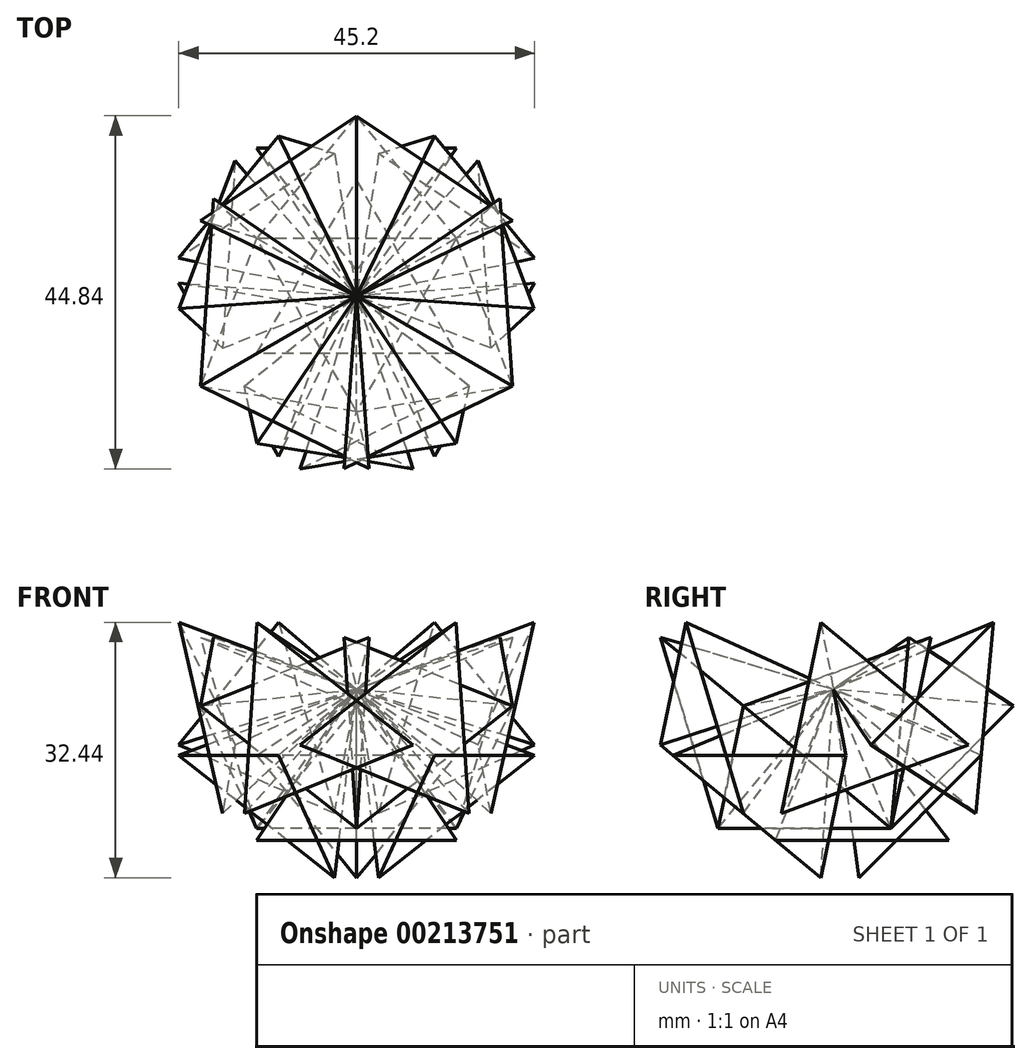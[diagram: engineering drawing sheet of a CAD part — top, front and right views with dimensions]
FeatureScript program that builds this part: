
annotation { "Feature Type Name" : "Feature", "Feature Type Description" : "" }
export const myFeature = defineFeature(function(context is Context, id is Id, definition is map)
    precondition{}
    {
        {
            assignVariable(context, id + "F0", {"name" : "a", "anyValue" : 1});
        }
        {
            assignVariable(context, id + "F1", {"name" : "phi", "anyValue" : getVariable(context, 'a') * (1 + sqrt(5)) / 2});
        }
        {
            assignVariable(context, id + "F2", {"name" : "h", "anyValue" : (sqrt(3) / 3) * (getVariable(context, 'a') + getVariable(context, 'a') * getVariable(context, 'phi'))});
        }
        {
            var Q0;
            Q0=qCreatedBy(makeId("Top.planeOp"),FACE);
            var sketch = newSketch(context, id + "F3", { "sketchPlane" : qUnion([Q0])});
            skCircle(sketch, "E0.cCircle", {"center": v(0, 0) * mm, "radius": 14.66 * mm, "construction": true});
            skLineSegment(sketch, "E0.0", {"start": v(0, 14.66) * mm, "end": v(12.7, -7.33) * mm});
            skLineSegment(sketch, "E0.1", {"start": v(12.7, -7.33) * mm, "end": v(-12.7, -7.33) * mm});
            skLineSegment(sketch, "E0.2", {"start": v(-12.7, -7.33) * mm, "end": v(0, 14.66) * mm});
            skSolve(sketch);
        }
        {
            var Q0;
            Q0=qCreatedBy(makeId("Top.planeOp"),FACE);
            cPlane(context, id + "F4", {"entities" : qUnion([Q0]), "cplaneType" : CPlaneType.OFFSET, "offset" : (getVariable(context, 'h')) * mm, "width" : 152.4 * mm, "height" : 152.4 * mm});
        }
        {
            var Q0;
            Q0=qCreatedBy(id+"F4.planeOp",FACE);
            var sketch = newSketch(context, id + "F5", { "sketchPlane" : qUnion([Q0])});
            skCircle(sketch, "E1.cCircle", {"center": v(0, 0) * mm, "radius": 14.66 * mm, "construction": true});
            skLineSegment(sketch, "E1.0", {"start": v(0, -14.66) * mm, "end": v(-12.7, 7.33) * mm});
            skLineSegment(sketch, "E1.1", {"start": v(-12.7, 7.33) * mm, "end": v(12.7, 7.33) * mm});
            skLineSegment(sketch, "E1.2", {"start": v(12.7, 7.33) * mm, "end": v(0, -14.66) * mm});
            skSolve(sketch);
        }
        {
            var Q0;
            Q0=qCreatedBy(makeId("Front.planeOp"),FACE);
            var sketch = newSketch(context, id + "F6", { "sketchPlane" : qUnion([Q0])});
            skLineSegment(sketch, "E2", {"start": v(0, 0) * mm, "end": v(0, 38.4) * mm});
            skPoint(sketch, "E3", {"position": v(0, 19.2) * mm});
            skSolve(sketch);
        }
        {
            var Q0;
            Q0=makeQuery(id+"F5.imprint","IMPRINT",FACE,{"disambiguationData":[TD([[makeQuery(id+"F5.imprint","IMPRINT",EDGE,{"derivedFrom":sQuery(id+"F5.wireOp",EDGE,"E1.0")}),-1.0]])]});
            var Q1;
            Q1=sQuery(id+"F6.wireOp",VERTEX,"E3");
            loft(context, id + "F7", {"sheetProfilesArray" : [{ "sheetProfileEntities" : qUnion([Q0]) }, { "sheetProfileEntities" : qUnion([Q1]) }]});
        }
        {
            var Q0;
            Q0=makeQuery(id+"F3.imprint","IMPRINT",FACE,{"disambiguationData":[TD([[makeQuery(id+"F3.imprint","IMPRINT",EDGE,{"derivedFrom":sQuery(id+"F3.wireOp",EDGE,"E0.0")}),-1.0]])]});
            var Q1;
            Q1=sQuery(id+"F6.wireOp",VERTEX,"E3");
            loft(context, id + "F8", {"sheetProfilesArray" : [{ "sheetProfileEntities" : qUnion([Q0]) }, { "sheetProfileEntities" : qUnion([Q1]) }]});
        }
        {
            var Q0;
            Q0=makeQuery(id+"F7.opLoft","SWEPT_BODY",BODY,{"disambiguationData":[OSD([makeQuery(id+"F5.imprint","IMPRINT",FACE,{"disambiguationData":[TD([[makeQuery(id+"F5.imprint","IMPRINT",EDGE,{"derivedFrom":sQuery(id+"F5.wireOp",EDGE,"E1.0")}),-1.0]])]}),sQuery(id+"F6.wireOp",VERTEX,"E3")])]});
            var Q1;
            Q1=makeQuery(id+"F8.opLoft","SWEPT_BODY",BODY,{"disambiguationData":[OSD([makeQuery(id+"F3.imprint","IMPRINT",FACE,{"disambiguationData":[TD([[makeQuery(id+"F3.imprint","IMPRINT",EDGE,{"derivedFrom":sQuery(id+"F3.wireOp",EDGE,"E0.0")}),-1.0]])]}),sQuery(id+"F6.wireOp",VERTEX,"E3")])]});
            var Q2;
            {var subQ0=sQuery(id+"F5.wireOp",EDGE,"E1.2");var subQ1=sQuery(id+"F5.wireOp",EDGE,"E1.1");var subQ2=sQuery(id+"F5.wireOp",EDGE,"E1.0");Q2=makeQuery(id+"F7.opLoft","SWEPT_FACE",FACE,{"disambiguationData":[OSD([subQ2,subQ1,subQ0]),TDD([makeQuery(id+"F5.imprint","INTERSECT",VERTEX,{"derivedFrom":[subQ2,subQ0]}),makeQuery(id+"F5.imprint","INTERSECT",VERTEX,{"derivedFrom":[subQ1,subQ0]}),makeQuery(id+"F5.imprint","IMPRINT",EDGE,{"derivedFrom":subQ0})])]});}
            mirror(context, id + "F9", {"entities" : qUnion([Q0, Q1]), "mirrorPlane" : qUnion([Q2])});
        }
        {
            var Q0;
            Q0=makeQuery(id+"F7.opLoft","SWEPT_BODY",BODY,{"disambiguationData":[OSD([makeQuery(id+"F5.imprint","IMPRINT",FACE,{"disambiguationData":[TD([[makeQuery(id+"F5.imprint","IMPRINT",EDGE,{"derivedFrom":sQuery(id+"F5.wireOp",EDGE,"E1.0")}),-1.0]])]}),sQuery(id+"F6.wireOp",VERTEX,"E3")])]});
            var Q1;
            Q1=makeQuery(id+"F8.opLoft","SWEPT_BODY",BODY,{"disambiguationData":[OSD([makeQuery(id+"F3.imprint","IMPRINT",FACE,{"disambiguationData":[TD([[makeQuery(id+"F3.imprint","IMPRINT",EDGE,{"derivedFrom":sQuery(id+"F3.wireOp",EDGE,"E0.0")}),-1.0]])]}),sQuery(id+"F6.wireOp",VERTEX,"E3")])]});
            var Q2;
            {var subQ0=sQuery(id+"F5.wireOp",EDGE,"E1.0");var subQ1=sQuery(id+"F5.wireOp",EDGE,"E1.1");var subQ2=sQuery(id+"F5.wireOp",EDGE,"E1.2");Q2=makeQuery(id+"F7.opLoft","SWEPT_FACE",FACE,{"disambiguationData":[OSD([subQ0,subQ1,subQ2]),TDD([makeQuery(id+"F5.imprint","INTERSECT",VERTEX,{"derivedFrom":[subQ0,subQ2]}),makeQuery(id+"F5.imprint","INTERSECT",VERTEX,{"derivedFrom":[subQ0,subQ1]}),makeQuery(id+"F5.imprint","IMPRINT",EDGE,{"derivedFrom":subQ0})])]});}
            mirror(context, id + "F10", {"entities" : qUnion([Q0, Q1]), "mirrorPlane" : qUnion([Q2])});
        }
        {
            var Q0;
            Q0=makeQuery(id+"F7.opLoft","SWEPT_BODY",BODY,{"disambiguationData":[OSD([makeQuery(id+"F5.imprint","IMPRINT",FACE,{"disambiguationData":[TD([[makeQuery(id+"F5.imprint","IMPRINT",EDGE,{"derivedFrom":sQuery(id+"F5.wireOp",EDGE,"E1.0")}),-1.0]])]}),sQuery(id+"F6.wireOp",VERTEX,"E3")])]});
            var Q1;
            Q1=makeQuery(id+"F8.opLoft","SWEPT_BODY",BODY,{"disambiguationData":[OSD([makeQuery(id+"F3.imprint","IMPRINT",FACE,{"disambiguationData":[TD([[makeQuery(id+"F3.imprint","IMPRINT",EDGE,{"derivedFrom":sQuery(id+"F3.wireOp",EDGE,"E0.0")}),-1.0]])]}),sQuery(id+"F6.wireOp",VERTEX,"E3")])]});
            var Q2;
            {var subQ0=sQuery(id+"F5.wireOp",EDGE,"E1.1");var subQ1=sQuery(id+"F5.wireOp",EDGE,"E1.2");var subQ2=sQuery(id+"F5.wireOp",EDGE,"E1.0");Q2=makeQuery(id+"F7.opLoft","SWEPT_FACE",FACE,{"disambiguationData":[OSD([subQ2,subQ0,subQ1]),TDD([makeQuery(id+"F5.imprint","INTERSECT",VERTEX,{"derivedFrom":[subQ2,subQ0]}),makeQuery(id+"F5.imprint","INTERSECT",VERTEX,{"derivedFrom":[subQ0,subQ1]}),makeQuery(id+"F5.imprint","IMPRINT",EDGE,{"derivedFrom":subQ0})])]});}
            mirror(context, id + "F11", {"entities" : qUnion([Q0, Q1]), "mirrorPlane" : qUnion([Q2])});
        }
        {
            var Q0;
            Q0=makeQuery(id+"F10.opPattern","COPY",BODY,{"derivedFrom":makeQuery(id+"F7.opLoft","SWEPT_BODY",BODY,{"disambiguationData":[OSD([makeQuery(id+"F5.imprint","IMPRINT",FACE,{"disambiguationData":[TD([[makeQuery(id+"F5.imprint","IMPRINT",EDGE,{"derivedFrom":sQuery(id+"F5.wireOp",EDGE,"E1.0")}),-1.0]])]}),sQuery(id+"F6.wireOp",VERTEX,"E3")])]}),"instanceName":"1"});
            var Q1;
            Q1=makeQuery(id+"F10.opPattern","COPY",BODY,{"derivedFrom":makeQuery(id+"F8.opLoft","SWEPT_BODY",BODY,{"disambiguationData":[OSD([makeQuery(id+"F3.imprint","IMPRINT",FACE,{"disambiguationData":[TD([[makeQuery(id+"F3.imprint","IMPRINT",EDGE,{"derivedFrom":sQuery(id+"F3.wireOp",EDGE,"E0.0")}),-1.0]])]}),sQuery(id+"F6.wireOp",VERTEX,"E3")])]}),"instanceName":"1"});
            var Q2;
            {var subQ0=sQuery(id+"F5.wireOp",EDGE,"E1.2");var subQ1=sQuery(id+"F5.wireOp",EDGE,"E1.1");var subQ2=sQuery(id+"F5.wireOp",EDGE,"E1.0");Q2=makeQuery(id+"F10.opPattern","COPY",FACE,{"derivedFrom":makeQuery(id+"F7.opLoft","SWEPT_FACE",FACE,{"disambiguationData":[OSD([subQ2,subQ1,subQ0]),TDD([makeQuery(id+"F5.imprint","INTERSECT",VERTEX,{"derivedFrom":[subQ2,subQ0]}),makeQuery(id+"F5.imprint","INTERSECT",VERTEX,{"derivedFrom":[subQ1,subQ0]}),makeQuery(id+"F5.imprint","IMPRINT",EDGE,{"derivedFrom":subQ0})])]}),"instanceName":"1"});}
            mirror(context, id + "F12", {"entities" : qUnion([Q0, Q1]), "mirrorPlane" : qUnion([Q2])});
        }
        {
            var Q0;
            Q0=makeQuery(id+"F9.opPattern","COPY",BODY,{"derivedFrom":makeQuery(id+"F7.opLoft","SWEPT_BODY",BODY,{"disambiguationData":[OSD([makeQuery(id+"F5.imprint","IMPRINT",FACE,{"disambiguationData":[TD([[makeQuery(id+"F5.imprint","IMPRINT",EDGE,{"derivedFrom":sQuery(id+"F5.wireOp",EDGE,"E1.0")}),-1.0]])]}),sQuery(id+"F6.wireOp",VERTEX,"E3")])]}),"instanceName":"1"});
            var Q1;
            Q1=makeQuery(id+"F9.opPattern","COPY",BODY,{"derivedFrom":makeQuery(id+"F8.opLoft","SWEPT_BODY",BODY,{"disambiguationData":[OSD([makeQuery(id+"F3.imprint","IMPRINT",FACE,{"disambiguationData":[TD([[makeQuery(id+"F3.imprint","IMPRINT",EDGE,{"derivedFrom":sQuery(id+"F3.wireOp",EDGE,"E0.0")}),-1.0]])]}),sQuery(id+"F6.wireOp",VERTEX,"E3")])]}),"instanceName":"1"});
            var Q2;
            {var subQ0=sQuery(id+"F5.wireOp",EDGE,"E1.0");var subQ1=sQuery(id+"F5.wireOp",EDGE,"E1.1");var subQ2=sQuery(id+"F5.wireOp",EDGE,"E1.2");Q2=makeQuery(id+"F9.opPattern","COPY",FACE,{"derivedFrom":makeQuery(id+"F7.opLoft","SWEPT_FACE",FACE,{"disambiguationData":[OSD([subQ0,subQ1,subQ2]),TDD([makeQuery(id+"F5.imprint","INTERSECT",VERTEX,{"derivedFrom":[subQ0,subQ2]}),makeQuery(id+"F5.imprint","INTERSECT",VERTEX,{"derivedFrom":[subQ0,subQ1]}),makeQuery(id+"F5.imprint","IMPRINT",EDGE,{"derivedFrom":subQ0})])]}),"instanceName":"1"});}
            mirror(context, id + "F13", {"entities" : qUnion([Q0, Q1]), "mirrorPlane" : qUnion([Q2])});
        }
        {
            var Q0;
            Q0=makeQuery(id+"F10.opPattern","COPY",BODY,{"derivedFrom":makeQuery(id+"F7.opLoft","SWEPT_BODY",BODY,{"disambiguationData":[OSD([makeQuery(id+"F5.imprint","IMPRINT",FACE,{"disambiguationData":[TD([[makeQuery(id+"F5.imprint","IMPRINT",EDGE,{"derivedFrom":sQuery(id+"F5.wireOp",EDGE,"E1.0")}),-1.0]])]}),sQuery(id+"F6.wireOp",VERTEX,"E3")])]}),"instanceName":"1"});
            var Q1;
            Q1=makeQuery(id+"F10.opPattern","COPY",BODY,{"derivedFrom":makeQuery(id+"F8.opLoft","SWEPT_BODY",BODY,{"disambiguationData":[OSD([makeQuery(id+"F3.imprint","IMPRINT",FACE,{"disambiguationData":[TD([[makeQuery(id+"F3.imprint","IMPRINT",EDGE,{"derivedFrom":sQuery(id+"F3.wireOp",EDGE,"E0.0")}),-1.0]])]}),sQuery(id+"F6.wireOp",VERTEX,"E3")])]}),"instanceName":"1"});
            var Q2;
            {var subQ0=sQuery(id+"F5.wireOp",EDGE,"E1.1");var subQ1=sQuery(id+"F5.wireOp",EDGE,"E1.2");var subQ2=sQuery(id+"F5.wireOp",EDGE,"E1.0");Q2=makeQuery(id+"F10.opPattern","COPY",FACE,{"derivedFrom":makeQuery(id+"F7.opLoft","SWEPT_FACE",FACE,{"disambiguationData":[OSD([subQ2,subQ0,subQ1]),TDD([makeQuery(id+"F5.imprint","INTERSECT",VERTEX,{"derivedFrom":[subQ2,subQ0]}),makeQuery(id+"F5.imprint","INTERSECT",VERTEX,{"derivedFrom":[subQ0,subQ1]}),makeQuery(id+"F5.imprint","IMPRINT",EDGE,{"derivedFrom":subQ0})])]}),"instanceName":"1"});}
            mirror(context, id + "F14", {"entities" : qUnion([Q0, Q1]), "mirrorPlane" : qUnion([Q2])});
        }
        {
            var Q0;
            Q0=makeQuery(id+"F11.opPattern","COPY",BODY,{"derivedFrom":makeQuery(id+"F7.opLoft","SWEPT_BODY",BODY,{"disambiguationData":[OSD([makeQuery(id+"F5.imprint","IMPRINT",FACE,{"disambiguationData":[TD([[makeQuery(id+"F5.imprint","IMPRINT",EDGE,{"derivedFrom":sQuery(id+"F5.wireOp",EDGE,"E1.0")}),-1.0]])]}),sQuery(id+"F6.wireOp",VERTEX,"E3")])]}),"instanceName":"1"});
            var Q1;
            Q1=makeQuery(id+"F11.opPattern","COPY",BODY,{"derivedFrom":makeQuery(id+"F8.opLoft","SWEPT_BODY",BODY,{"disambiguationData":[OSD([makeQuery(id+"F3.imprint","IMPRINT",FACE,{"disambiguationData":[TD([[makeQuery(id+"F3.imprint","IMPRINT",EDGE,{"derivedFrom":sQuery(id+"F3.wireOp",EDGE,"E0.0")}),-1.0]])]}),sQuery(id+"F6.wireOp",VERTEX,"E3")])]}),"instanceName":"1"});
            var Q2;
            {var subQ0=sQuery(id+"F5.wireOp",EDGE,"E1.0");var subQ1=sQuery(id+"F5.wireOp",EDGE,"E1.1");var subQ2=sQuery(id+"F5.wireOp",EDGE,"E1.2");Q2=makeQuery(id+"F11.opPattern","COPY",FACE,{"derivedFrom":makeQuery(id+"F7.opLoft","SWEPT_FACE",FACE,{"disambiguationData":[OSD([subQ0,subQ1,subQ2]),TDD([makeQuery(id+"F5.imprint","INTERSECT",VERTEX,{"derivedFrom":[subQ0,subQ2]}),makeQuery(id+"F5.imprint","INTERSECT",VERTEX,{"derivedFrom":[subQ0,subQ1]}),makeQuery(id+"F5.imprint","IMPRINT",EDGE,{"derivedFrom":subQ0})])]}),"instanceName":"1"});}
            mirror(context, id + "F15", {"entities" : qUnion([Q0, Q1]), "mirrorPlane" : qUnion([Q2])});
        }
        {
            var Q0;
            Q0=makeQuery(id+"F9.opPattern","COPY",BODY,{"derivedFrom":makeQuery(id+"F7.opLoft","SWEPT_BODY",BODY,{"disambiguationData":[OSD([makeQuery(id+"F5.imprint","IMPRINT",FACE,{"disambiguationData":[TD([[makeQuery(id+"F5.imprint","IMPRINT",EDGE,{"derivedFrom":sQuery(id+"F5.wireOp",EDGE,"E1.0")}),-1.0]])]}),sQuery(id+"F6.wireOp",VERTEX,"E3")])]}),"instanceName":"1"});
            var Q1;
            Q1=makeQuery(id+"F9.opPattern","COPY",BODY,{"derivedFrom":makeQuery(id+"F8.opLoft","SWEPT_BODY",BODY,{"disambiguationData":[OSD([makeQuery(id+"F3.imprint","IMPRINT",FACE,{"disambiguationData":[TD([[makeQuery(id+"F3.imprint","IMPRINT",EDGE,{"derivedFrom":sQuery(id+"F3.wireOp",EDGE,"E0.0")}),-1.0]])]}),sQuery(id+"F6.wireOp",VERTEX,"E3")])]}),"instanceName":"1"});
            var Q2;
            {var subQ0=sQuery(id+"F5.wireOp",EDGE,"E1.1");var subQ1=sQuery(id+"F5.wireOp",EDGE,"E1.2");var subQ2=sQuery(id+"F5.wireOp",EDGE,"E1.0");Q2=makeQuery(id+"F9.opPattern","COPY",FACE,{"derivedFrom":makeQuery(id+"F7.opLoft","SWEPT_FACE",FACE,{"disambiguationData":[OSD([subQ2,subQ0,subQ1]),TDD([makeQuery(id+"F5.imprint","INTERSECT",VERTEX,{"derivedFrom":[subQ2,subQ0]}),makeQuery(id+"F5.imprint","INTERSECT",VERTEX,{"derivedFrom":[subQ0,subQ1]}),makeQuery(id+"F5.imprint","IMPRINT",EDGE,{"derivedFrom":subQ0})])]}),"instanceName":"1"});}
            mirror(context, id + "F16", {"entities" : qUnion([Q0, Q1]), "mirrorPlane" : qUnion([Q2])});
        }
        {
            var Q0;
            Q0=makeQuery(id+"F11.opPattern","COPY",BODY,{"derivedFrom":makeQuery(id+"F7.opLoft","SWEPT_BODY",BODY,{"disambiguationData":[OSD([makeQuery(id+"F5.imprint","IMPRINT",FACE,{"disambiguationData":[TD([[makeQuery(id+"F5.imprint","IMPRINT",EDGE,{"derivedFrom":sQuery(id+"F5.wireOp",EDGE,"E1.0")}),-1.0]])]}),sQuery(id+"F6.wireOp",VERTEX,"E3")])]}),"instanceName":"1"});
            var Q1;
            Q1=makeQuery(id+"F11.opPattern","COPY",BODY,{"derivedFrom":makeQuery(id+"F8.opLoft","SWEPT_BODY",BODY,{"disambiguationData":[OSD([makeQuery(id+"F3.imprint","IMPRINT",FACE,{"disambiguationData":[TD([[makeQuery(id+"F3.imprint","IMPRINT",EDGE,{"derivedFrom":sQuery(id+"F3.wireOp",EDGE,"E0.0")}),-1.0]])]}),sQuery(id+"F6.wireOp",VERTEX,"E3")])]}),"instanceName":"1"});
            var Q2;
            {var subQ0=sQuery(id+"F5.wireOp",EDGE,"E1.2");var subQ1=sQuery(id+"F5.wireOp",EDGE,"E1.1");var subQ2=sQuery(id+"F5.wireOp",EDGE,"E1.0");Q2=makeQuery(id+"F11.opPattern","COPY",FACE,{"derivedFrom":makeQuery(id+"F7.opLoft","SWEPT_FACE",FACE,{"disambiguationData":[OSD([subQ2,subQ1,subQ0]),TDD([makeQuery(id+"F5.imprint","INTERSECT",VERTEX,{"derivedFrom":[subQ2,subQ0]}),makeQuery(id+"F5.imprint","INTERSECT",VERTEX,{"derivedFrom":[subQ1,subQ0]}),makeQuery(id+"F5.imprint","IMPRINT",EDGE,{"derivedFrom":subQ0})])]}),"instanceName":"1"});}
            mirror(context, id + "F17", {"entities" : qUnion([Q0, Q1]), "mirrorPlane" : qUnion([Q2])});
        }
    });
